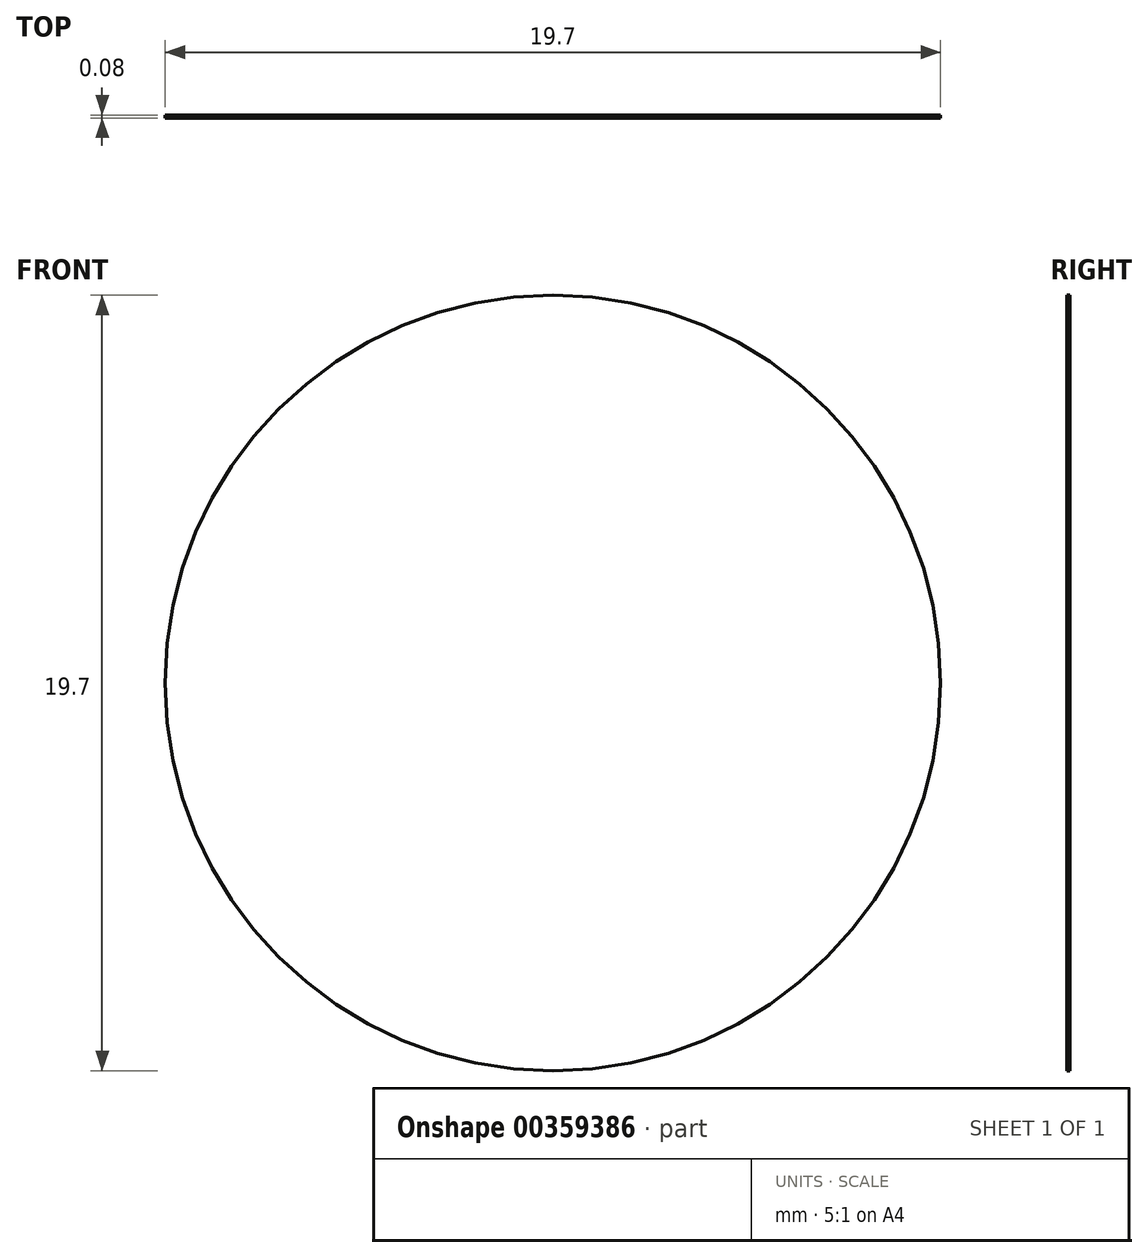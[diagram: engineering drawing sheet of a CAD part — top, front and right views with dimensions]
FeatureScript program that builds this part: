
annotation { "Feature Type Name" : "Feature", "Feature Type Description" : "" }
export const myFeature = defineFeature(function(context is Context, id is Id, definition is map)
    precondition{}
    {
        {
            var Q0;
            Q0=qCreatedBy(makeId("Front.planeOp"),FACE);
            var sketch = newSketch(context, id + "F0", { "sketchPlane" : qUnion([Q0])});
            skCircle(sketch, "E0", {"center": v(0, 0) * mm, "radius": 9.85 * mm});
            skSolve(sketch);
        }
        {
            var Q0;
            Q0 = qSketchRegion(id + "F0", true);
            extrude(context, id + "F1", {"entities" : qUnion([Q0]), "depth" : 0.07 * mm});
        }
    });
